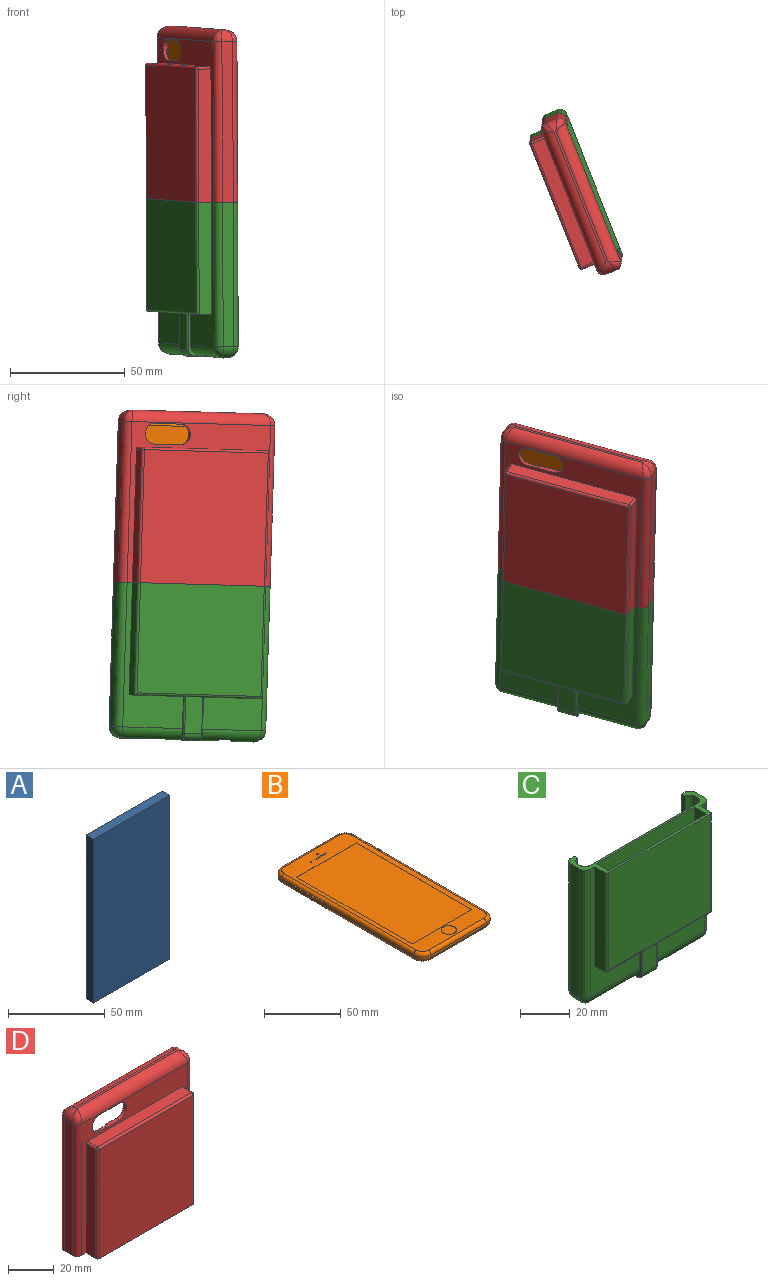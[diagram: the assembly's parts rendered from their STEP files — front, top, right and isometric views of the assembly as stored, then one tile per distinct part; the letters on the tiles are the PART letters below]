
ASSEMBLY  parts=4 mates=4
PART A: 11 faces, bbox 55.5x5.5x103.5 mm
  f0: plane 55.5x5.5mm, normal (0,0,-1), area 279mm2, adj f2,f3,f4,f5,f6,f7,f8,f9
  f1: plane 55.5x5.5mm, normal (0,0,1), area 305.2mm2, adj f2,f3,f4,f5
  f2: plane 103.5x5.5mm, normal (-1,0,0), area 569.2mm2, adj f0,f1,f4,f5
  f3: plane 103.5x5.5mm, normal (1,0,0), area 569.2mm2, adj f0,f1,f4,f5
  f4: plane 103.5x55.5mm, normal (0,-1,0), area 5744.2mm2, adj f0,f1,f2,f3
  f5: plane 103.5x55.5mm, normal (0,1,0), area 5744.2mm2, adj f0,f1,f2,f3
  f6: plane 7.5x7.5mm, normal (0,1,0), area 56.2mm2, adj f0,f7,f9,f10
  f7: plane 7.5x3.5mm, normal (1,0,0), area 26.2mm2, adj f0,f6,f8,f10
  f8: plane 7.5x7.5mm, normal (0,-1,0), area 56.2mm2, adj f0,f7,f9,f10
  f9: plane 7.5x3.5mm, normal (-1,0,0), area 26.2mm2, adj f0,f6,f8,f10
  f10: plane 7.5x3.5mm, normal (0,0,-1), area 26.2mm2, adj f6,f7,f8,f9
PART B: 83 faces, bbox 69x139.3x7 mm
  f0: plane 12.52x2.01mm, normal (-1,0,0), area 24.1mm2, adj f6,f41,f53,f75,f76,f77
  f1: plane 2.92x2.01mm, normal (-1,0,0), area 4.3mm2, adj f41,f53,f64,f65,f66,f79,f80,f81
  f2: plane 97.29x2mm, normal (1,0,0), area 194.1mm2, adj f21,f34,f35,f36,f42,f54
  f3: plane 12.29x2mm, normal (1,0,0), area 24.1mm2, adj f4,f30,f31,f32,f49,f61
  f4: cylinder r=8mm len=8mm, axis (0,0,-1), area 25.1mm2, adj f3,f5,f47,f59
  f5: plane 51x2mm, normal (0,1,0), area 102mm2, adj f4,f6,f45,f57
  f6: cylinder r=8mm len=8mm, axis (0,0,-1), area 25.1mm2, adj f0,f5,f43,f55
  f7: plane 79.91x2mm, normal (-1,0,0), area 159.1mm2, adj f8,f41,f53,f68,f69,f70
  f8: cylinder r=8mm len=8mm, axis (0,0,-1), area 25.1mm2, adj f7,f9,f39,f51
  f9: plane 51x2mm, normal (0,-1,0), area 102mm2, adj f8,f21,f38,f50
  f10: plane 1x0.05mm, normal (1,0,0), area 0.1mm2, adj f11,f16,f22,f26
  f11: plane 10x0.05mm, normal (0,-1,0), area 0.5mm2, adj f10,f12,f22,f26
  f12: plane 1x0.05mm, normal (-1,0,0), area 0.1mm2, adj f11,f16,f22,f26
  f13: plane 55x0.05mm, normal (0,1,0), area 2.8mm2, adj f14,f20,f22,f24
  f14: plane 106.54x0.05mm, normal (1,0,0), area 5.3mm2, adj f13,f15,f22,f24
  f15: plane 55x0.05mm, normal (0,-1,0), area 2.8mm2, adj f14,f20,f22,f24
  f16: plane 10x0.05mm, normal (0,1,0), area 0.5mm2, adj f10,f12,f22,f26
  f17: cylinder r=5mm len=10mm, axis (0,0,-1), area 1.6mm2, adj f22,f25
  f18: cylinder r=0.5mm len=1mm, axis (0,0,-1), area 0.2mm2, adj f22,f27
  f19: cylinder r=0.5mm len=1mm, axis (0,0,-1), area 0.2mm2, adj f22,f28
  f20: plane 106.5x0.05mm, normal (-1,0,0), area 5.3mm2, adj f13,f15,f22,f24
  f21: cylinder r=8mm len=8mm, axis (0,0,-1), area 25.1mm2, adj f2,f9,f40,f52
  f22: plane 133x62.03mm, normal (0,0,1), area 2271.7mm2, adj f10,f11,f12,f13,f14,f15,f16,f17
  f23: plane 133x62.02mm, normal (0,0,-1), area 8220.2mm2, adj f50,f51,f52,f53,f54,f55,f56,f57
  f24: plane 106.54x55mm, normal (0,0,1), area 5858.6mm2, adj f13,f14,f15,f20
  f25: plane 10x10mm, normal (0,0,1), area 78.5mm2, adj f17
  f26: plane 10x1mm, normal (0,0,1), area 10mm2, adj f10,f11,f12,f16
  f27: plane 1x1mm, normal (0,0,1), area 0.8mm2, adj f18
  f28: plane 1x1mm, normal (0,0,1), area 0.8mm2, adj f19
  f29: plane 11x1mm, normal (0,0,-1), area 11mm2, adj f30,f36,f37,f58
  f30: cylinder r=1mm len=1mm, axis (-1,0,0), area 1.6mm2, adj f3,f29,f31,f37,f60
  f31: plane 1x0.7mm, normal (0,1,0), area 0.7mm2, adj f3,f30,f32,f37
  f32: cylinder r=1mm len=1mm, axis (-1,0,0), area 1.6mm2, adj f3,f31,f33,f37,f48
  f33: plane 11x1mm, normal (0,0,1), area 11mm2, adj f32,f34,f37,f46
  f34: cylinder r=1mm len=1mm, axis (-1,0,0), area 1.6mm2, adj f2,f33,f35,f37,f44
  f35: plane 1x0.7mm, normal (0,-1,0), area 0.7mm2, adj f2,f34,f36,f37
  f36: cylinder r=1mm len=1mm, axis (-1,0,0), area 1.6mm2, adj f2,f29,f35,f37,f56
  f37: plane 13x2.7mm, normal (1,0,0), area 34.2mm2, adj f29,f30,f31,f32,f33,f34,f35,f36
  f38: cylinder r=2.5mm len=51mm, axis (-1,0,0), area 200.3mm2, adj f9,f22,f39,f40
  f39: torus R=5.5mm, axis (0,0,1), area 43.7mm2, adj f8,f22,f38,f41
  f40: torus R=5.5mm, axis (0,0,1), area 43.7mm2, adj f21,f22,f38,f42
  f41: cylinder r=2.5mm len=122mm, axis (0,1,0), area 479.1mm2, adj f0,f1,f7,f22,f39,f43,f62,f73
  f42: cylinder r=2.5mm len=97.2mm, axis (0,-1,0), area 381.7mm2, adj f2,f22,f40,f44
  f43: torus R=5.5mm, axis (0,0,1), area 43.7mm2, adj f6,f22,f41,f45
  f44: bspline ~2.55x2.54mm, area 2.9mm2, adj f22,f34,f42,f46
  f45: cylinder r=2.5mm len=51mm, axis (1,0,0), area 200.3mm2, adj f5,f22,f43,f47
  f46: cylinder r=2.5mm len=11mm, axis (0,1,0), area 38.8mm2, adj f22,f33,f44,f48
  f47: torus R=5.5mm, axis (0,0,1), area 43.7mm2, adj f4,f22,f45,f49
  f48: bspline ~2.57x2.57mm, area 2.9mm2, adj f22,f32,f46,f49
  f49: cylinder r=2.5mm len=12.2mm, axis (0,-1,0), area 47.9mm2, adj f3,f22,f47,f48
  f50: cylinder r=2.5mm len=51mm, axis (1,0,0), area 200.3mm2, adj f9,f23,f51,f52
  f51: torus R=5.5mm, axis (0,0,1), area 43.7mm2, adj f8,f23,f50,f53
  f52: torus R=5.5mm, axis (0,0,1), area 43.7mm2, adj f21,f23,f50,f54
  f53: cylinder r=2.5mm len=122mm, axis (0,-1,0), area 477.5mm2, adj f0,f1,f7,f23,f51,f55,f72,f77
  f54: cylinder r=2.5mm len=97.29mm, axis (0,1,0), area 382mm2, adj f2,f23,f52,f56
  f55: torus R=5.5mm, axis (0,0,1), area 43.7mm2, adj f6,f23,f53,f57
  f56: bspline ~2.67x2.66mm, area 2.7mm2, adj f23,f36,f54,f58
  f57: cylinder r=2.5mm len=51mm, axis (-1,0,0), area 200.3mm2, adj f5,f23,f55,f59
  f58: cylinder r=2.5mm len=11mm, axis (0,1,0), area 39.9mm2, adj f23,f29,f56,f60
  f59: torus R=5.5mm, axis (0,0,1), area 43.7mm2, adj f4,f23,f57,f61
  f60: bspline ~2.57x2.56mm, area 2.7mm2, adj f23,f30,f58,f61
  f61: cylinder r=2.5mm len=12.29mm, axis (0,1,0), area 48.2mm2, adj f3,f23,f59,f60
  f62: plane 14.23x0.5mm, normal (1,0,0), area 6.9mm2, adj f41,f63,f64,f70
  f63: plane 12.49x1mm, normal (0,0,1), area 12.5mm2, adj f62,f64,f70,f71
  f64: cylinder r=1mm len=1mm, axis (1,0,0), area 1.6mm2, adj f1,f62,f63,f65,f71
  f65: plane 1x0.7mm, normal (0,1,0), area 0.7mm2, adj f1,f64,f66,f71
  f66: cylinder r=1mm len=1mm, axis (1,0,0), area 1.6mm2, adj f1,f65,f67,f71,f72
  f67: plane 12.49x1mm, normal (0,0,-1), area 12.5mm2, adj f66,f68,f71,f72
  f68: cylinder r=1mm len=1mm, axis (1,0,0), area 1.6mm2, adj f7,f67,f69,f71,f72
  f69: plane 1x0.7mm, normal (0,-1,0), area 0.7mm2, adj f7,f68,f70,f71
  f70: cylinder r=1mm len=1mm, axis (1,0,0), area 1.6mm2, adj f7,f62,f63,f69,f71
  f71: plane 14.49x2.7mm, normal (-1,0,0), area 38.3mm2, adj f63,f64,f65,f66,f67,f68,f69,f70
  f72: plane 13.69x0.2mm, normal (1,0,0), area 2.7mm2, adj f53,f66,f67,f68
  f73: plane 13.81x0.57mm, normal (1,0,0), area 7.6mm2, adj f41,f74,f75,f81
  f74: plane 12x1mm, normal (0,0,1), area 12mm2, adj f73,f75,f81,f82
  f75: cylinder r=1mm len=1mm, axis (1,0,0), area 1.6mm2, adj f0,f73,f74,f76,f82
  f76: plane 1x0.7mm, normal (0,1,0), area 0.7mm2, adj f0,f75,f77,f82
  f77: cylinder r=1mm len=1mm, axis (1,0,0), area 1.6mm2, adj f0,f53,f76,f78,f82
  f78: plane 12.01x1.01mm, normal (0,0,-1), area 12mm2, adj f53,f77,f79,f82
  f79: cylinder r=1mm len=1mm, axis (1,0,0), area 1.6mm2, adj f1,f53,f78,f80,f82
  f80: plane 1x0.7mm, normal (0,-1,0), area 0.7mm2, adj f1,f79,f81,f82
  f81: cylinder r=1mm len=1mm, axis (1,0,0), area 1.6mm2, adj f1,f73,f74,f80,f82
  f82: plane 14x2.7mm, normal (-1,0,0), area 36.9mm2, adj f74,f75,f76,f77,f78,f79,f80,f81
PART C: 93 faces, bbox 71x18x68.2 mm
  f0: cylinder r=5mm len=28.5mm, axis (1,0,0), area 188.9mm2, adj f5,f7,f28,f33,f52,f53,f54,f83
  f1: plane 63x28mm, normal (0,-1,0), area 514.5mm2, adj f2,f4,f10,f25,f66,f84
  f2: plane 60x6mm, normal (0,0,-1), area 346.6mm2, adj f1,f5,f65,f66,f82,f83,f84,f85
  f3: plane 56x7mm, normal (0,0,1), area 382.5mm2, adj f64,f67,f68,f69,f70,f71,f72,f73
  f4: plane 71x18mm, normal (0,0,1), area 217.6mm2, adj f1,f5,f11,f12,f13,f14,f15,f16
  f5: plane 63x28mm, normal (0,-1,0), area 514.5mm2, adj f0,f2,f4,f24,f65,f83
  f6: plane 67x7mm, normal (0,0,1), area 383.7mm2, adj f14,f15,f16,f17,f18,f19,f20,f35
  f7: plane 23x4.5mm, normal (0,0,-1), area 51mm2, adj f0,f9,f10,f46,f52,f86,f87,f91
  f8: plane 9x1mm, normal (0,0,-1), area 9mm2, adj f9,f10,f29,f48
  f9: cylinder r=5mm len=65mm, axis (-1,0,0), area 452.3mm2, adj f7,f8,f13,f21,f28,f30,f32,f36
  f10: cylinder r=5mm len=28.5mm, axis (1,0,0), area 193.8mm2, adj f1,f7,f8,f31,f46,f48,f49,f84
  f11: plane 63x2mm, normal (-1,0,0), area 126mm2, adj f4,f13,f14,f36
  f12: plane 63x2mm, normal (1,0,0), area 126mm2, adj f4,f20,f21,f36
  f13: plane 63x2mm, normal (0,1,0), area 126mm2, adj f4,f9,f11,f27
  f14: cylinder r=3mm len=65mm, axis (0,0,1), area 306.3mm2, adj f4,f6,f11,f15,f35
  f15: plane 65x1mm, normal (-1,0,0), area 65mm2, adj f4,f6,f14,f16
  f16: cylinder r=3mm len=65mm, axis (0,0,1), area 306.3mm2, adj f4,f6,f15,f17
  f17: plane 65x61mm, normal (0,1,0), area 3965mm2, adj f4,f6,f16,f18
  f18: cylinder r=3mm len=65mm, axis (0,0,1), area 306.3mm2, adj f4,f6,f17,f19
  f19: plane 65x1mm, normal (1,0,0), area 65mm2, adj f4,f6,f18,f20
  f20: cylinder r=3mm len=65mm, axis (0,0,1), area 306.3mm2, adj f4,f6,f12,f19,f35
  f21: plane 63x2mm, normal (0,1,0), area 126mm2, adj f4,f9,f12,f22
  f22: cylinder r=3mm len=63mm, axis (0,0,1), area 296.9mm2, adj f4,f21,f23,f32
  f23: plane 63x5mm, normal (-1,0,0), area 315mm2, adj f4,f22,f24,f34
  f24: cylinder r=3mm len=63mm, axis (0,0,1), area 296.9mm2, adj f4,f5,f23,f33
  f25: cylinder r=3mm len=63mm, axis (0,0,1), area 296.9mm2, adj f1,f4,f26,f31
  f26: plane 63x5mm, normal (1,0,0), area 315mm2, adj f4,f25,f27,f29
  f27: cylinder r=3mm len=63mm, axis (0,0,1), area 296.9mm2, adj f4,f13,f26,f30
  f28: plane 4x1mm, normal (0,0,-1), area 4mm2, adj f0,f9,f34,f54
  f29: cylinder r=5mm len=5mm, axis (0,1,0), area 27.9mm2, adj f8,f26,f30,f31
  f30: bspline ~6.03x5mm, area 24.5mm2, adj f9,f27,f29
  f31: bspline ~6.03x5mm, area 24.5mm2, adj f10,f25,f29
  f32: bspline ~6.03x5mm, area 24.5mm2, adj f9,f22,f34
  f33: bspline ~6.03x5mm, area 24.5mm2, adj f0,f24,f34
  f34: cylinder r=5mm len=5mm, axis (0,-1,0), area 27.9mm2, adj f23,f28,f32,f33
  f35: plane 61x2mm, normal (0,-1,0), area 122mm2, adj f6,f14,f20,f36
  f36: plane 61x2mm, normal (0,0,1), area 122mm2, adj f9,f11,f12,f35
  f37: plane 6x5.5mm, normal (0,1,0), area 33mm2, adj f6,f38,f44,f45
  f38: cylinder r=0.5mm len=6mm, axis (0,0,-1), area 4.7mm2, adj f6,f37,f39,f45
  f39: plane 6x0.5mm, normal (-1,0,0), area 3mm2, adj f6,f38,f40,f45
  f40: cylinder r=0.5mm len=6mm, axis (0,0,-1), area 4.7mm2, adj f6,f39,f41,f45
  f41: plane 6x5.5mm, normal (0,-1,0), area 33mm2, adj f6,f40,f42,f45
  f42: cylinder r=0.5mm len=6mm, axis (0,0,-1), area 4.7mm2, adj f6,f41,f43,f45
  f43: plane 6x0.5mm, normal (1,0,0), area 3mm2, adj f6,f42,f44,f45
  f44: cylinder r=0.5mm len=6mm, axis (0,0,-1), area 4.7mm2, adj f6,f37,f43,f45
  f45: plane 6.5x1.5mm, normal (0,0,1), area 9.5mm2, adj f37,f38,f39,f40,f41,f42,f43,f44
  f46: plane 6x1mm, normal (1,0,0), area 4.9mm2, adj f7,f9,f10,f47,f49,f50
  f47: plane 8x0.33mm, normal (0,-1,0), area 2.6mm2, adj f9,f46,f48,f50
  f48: plane 6x1mm, normal (-1,0,0), area 4.9mm2, adj f8,f9,f10,f47,f49,f50
  f49: plane 8x0.33mm, normal (0,1,0), area 2.6mm2, adj f10,f46,f48,f50
  f50: plane 8x6mm, normal (0,0,-1), area 18.7mm2, adj f46,f47,f48,f49,f60,f61,f62,f63
  f51: plane 17x0.77mm, normal (0,-1,0), area 13.1mm2, adj f9,f52,f54,f55
  f52: plane 4x1mm, normal (-1,0,0), area 3.8mm2, adj f0,f7,f9,f51,f53,f55
  f53: plane 17x0.77mm, normal (0,1,0), area 13.1mm2, adj f0,f52,f54,f55
  f54: plane 4x1mm, normal (1,0,0), area 3.8mm2, adj f0,f9,f28,f51,f53,f55
  f55: plane 17x4mm, normal (0,0,-1), area 29.3mm2, adj f51,f52,f53,f54,f56,f57,f58,f59
  f56: plane 15.5x2mm, normal (0,-1,0), area 31mm2, adj f6,f55,f58,f59
  f57: plane 15.5x2mm, normal (0,1,0), area 31mm2, adj f6,f55,f58,f59
  f58: plane 2.5x2mm, normal (-1,0,0), area 5mm2, adj f6,f55,f56,f57
  f59: plane 2.5x2mm, normal (1,0,0), area 5mm2, adj f6,f55,f56,f57
  f60: plane 6.5x2mm, normal (0,1,0), area 13mm2, adj f6,f50,f62,f63
  f61: plane 6.5x2mm, normal (0,-1,0), area 13mm2, adj f6,f50,f62,f63
  f62: plane 4.5x2mm, normal (1,0,0), area 9mm2, adj f6,f50,f60,f61
  f63: plane 4.5x2mm, normal (-1,0,0), area 9mm2, adj f6,f50,f60,f61
  f64: plane 47x7mm, normal (1,0,0), area 329mm2, adj f3,f4,f68,f79
  f65: plane 49x6mm, normal (-1,0,0), area 294mm2, adj f2,f4,f5,f80
  f66: plane 49x6mm, normal (1,0,0), area 294mm2, adj f1,f2,f4,f81
  f67: plane 47x7mm, normal (-1,0,0), area 329mm2, adj f3,f4,f68,f79
  f68: plane 56x47mm, normal (0,-1,0), area 2632mm2, adj f3,f4,f64,f67
  f69: plane 6x5.5mm, normal (0,1,0), area 33mm2, adj f3,f70,f76,f77
  f70: cylinder r=0.5mm len=6mm, axis (0,0,-1), area 4.7mm2, adj f3,f69,f71,f77
  f71: plane 6x0.5mm, normal (-1,0,0), area 3mm2, adj f3,f70,f72,f77
  f72: cylinder r=0.5mm len=6mm, axis (0,0,-1), area 4.7mm2, adj f3,f71,f73,f77
  f73: plane 6x5.5mm, normal (0,-1,0), area 33mm2, adj f3,f72,f74,f77
  f74: cylinder r=0.5mm len=6mm, axis (0,0,-1), area 4.7mm2, adj f3,f73,f75,f77
  f75: plane 6x0.5mm, normal (1,0,0), area 3mm2, adj f3,f74,f76,f77
  f76: cylinder r=0.5mm len=6mm, axis (0,0,-1), area 4.7mm2, adj f3,f69,f75,f77
  f77: plane 6.5x1.5mm, normal (0,0,1), area 9.5mm2, adj f69,f70,f71,f72,f73,f74,f75,f76
  f78: plane 58x48mm, normal (0,-1,0), area 2784mm2, adj f4,f80,f81,f82
  f79: plane 56x47mm, normal (0,1,0), area 2632mm2, adj f3,f4,f64,f67
  f80: cylinder r=1mm len=49mm, axis (0,0,1), area 76.4mm2, adj f4,f65,f78,f82
  f81: cylinder r=1mm len=49mm, axis (0,0,-1), area 76.4mm2, adj f4,f66,f78,f82
  f82: cylinder r=1mm len=60mm, axis (-1,0,0), area 93.1mm2, adj f2,f78,f80,f81
  f83: plane 18.5x3.82mm, normal (-1,0,0), area 20.8mm2, adj f0,f2,f5,f87,f88,f89
  f84: plane 18.5x3.82mm, normal (1,0,0), area 20.8mm2, adj f1,f2,f10,f90,f91,f92
  f85: plane 16x8mm, normal (0,-1,0), area 128mm2, adj f2,f86,f88,f90
  f86: cylinder r=3mm len=8mm, axis (1,0,0), area 37.7mm2, adj f7,f85,f89,f92
  f87: cylinder r=0.5mm len=3.5mm, axis (0,-1,0), area 1.9mm2, adj f0,f7,f83,f89
  f88: cylinder r=0.5mm len=16mm, axis (0,0,1), area 12.6mm2, adj f2,f83,f85,f89
  f89: torus R=2.5mm, axis (1,0,0), area 3.5mm2, adj f83,f86,f87,f88
  f90: cylinder r=0.5mm len=16mm, axis (0,0,-1), area 12.6mm2, adj f2,f84,f85,f92
  f91: cylinder r=0.5mm len=3.5mm, axis (0,1,0), area 1.9mm2, adj f7,f10,f84,f92
  f92: torus R=2.5mm, axis (1,0,0), area 3.5mm2, adj f84,f86,f90,f91
PART D: 54 faces, bbox 71x18x75 mm
  f0: plane 73x61mm, normal (0,1,0), area 3671.2mm2, adj f1,f2,f9,f10,f20,f48,f49,f50
  f1: plane 12.1x2mm, normal (0,0,1), area 21.4mm2, adj f0,f5,f48,f50,f52,f53
  f2: plane 67x7mm, normal (0,0,-1), area 461.3mm2, adj f0,f7,f8,f9,f10,f11,f12,f40
  f3: plane 70.5x2mm, normal (1,0,0), area 141mm2, adj f4,f12,f20,f38,f39
  f4: plane 70x2mm, normal (0,1,0), area 140mm2, adj f3,f14,f20,f38
  f5: plane 70x65mm, normal (0,-1,0), area 837.9mm2, adj f1,f16,f17,f20,f25,f26,f27,f31
  f6: plane 70.5x2mm, normal (-1,0,0), area 141mm2, adj f7,f13,f20,f38,f39
  f7: cylinder r=3mm len=73mm, axis (0,0,-1), area 344mm2, adj f2,f6,f8,f20,f40
  f8: plane 73x1mm, normal (-1,0,0), area 73mm2, adj f2,f7,f9,f20
  f9: cylinder r=3mm len=73mm, axis (0,0,-1), area 344mm2, adj f0,f2,f8,f20
  f10: cylinder r=3mm len=73mm, axis (0,0,-1), area 344mm2, adj f0,f2,f11,f20
  f11: plane 73x1mm, normal (1,0,0), area 73mm2, adj f2,f10,f12,f20
  f12: cylinder r=3mm len=73mm, axis (0,0,-1), area 344mm2, adj f2,f3,f11,f20,f40
  f13: plane 70x2mm, normal (0,1,0), area 140mm2, adj f6,f19,f20,f38
  f14: cylinder r=3mm len=70mm, axis (0,0,-1), area 329.9mm2, adj f4,f15,f20,f37
  f15: plane 70x5mm, normal (-1,0,0), area 350mm2, adj f14,f16,f20,f35
  f16: cylinder r=3mm len=70mm, axis (0,0,-1), area 329.9mm2, adj f5,f15,f20,f33
  f17: cylinder r=3mm len=70mm, axis (0,0,-1), area 329.9mm2, adj f5,f18,f20,f32
  f18: plane 70x5mm, normal (1,0,0), area 350mm2, adj f17,f19,f20,f34
  f19: cylinder r=3mm len=70mm, axis (0,0,-1), area 329.9mm2, adj f13,f18,f20,f36
  f20: plane 71x18mm, normal (0,0,-1), area 212.6mm2, adj f0,f3,f4,f5,f6,f7,f8,f9
  f21: plane 61x1mm, normal (0,0,1), area 61mm2, adj f31,f34,f35,f38
  f22: plane 57x7mm, normal (1,0,0), area 399mm2, adj f20,f23,f28,f29
  f23: plane 56x7mm, normal (0,0,-1), area 392mm2, adj f22,f24,f28,f29
  f24: plane 57x7mm, normal (-1,0,0), area 399mm2, adj f20,f23,f28,f29
  f25: plane 58x6mm, normal (1,0,0), area 348mm2, adj f5,f20,f45,f47
  f26: plane 58x6mm, normal (0,0,1), area 348mm2, adj f5,f42,f44,f45
  f27: plane 58x6mm, normal (-1,0,0), area 348mm2, adj f5,f20,f41,f42
  f28: plane 57x56mm, normal (0,-1,0), area 3192mm2, adj f20,f22,f23,f24
  f29: plane 57x56mm, normal (0,1,0), area 3192mm2, adj f20,f22,f23,f24
  f30: plane 58x58mm, normal (0,-1,0), area 3364mm2, adj f20,f41,f44,f47
  f31: cylinder r=5mm len=65mm, axis (-1,0,0), area 499.1mm2, adj f5,f21,f32,f33
  f32: bspline ~6.03x5mm, area 24.5mm2, adj f17,f31,f34
  f33: bspline ~6.03x5mm, area 24.5mm2, adj f16,f31,f35
  f34: cylinder r=5mm len=5mm, axis (0,-1,0), area 27.9mm2, adj f18,f21,f32,f36
  f35: cylinder r=5mm len=5mm, axis (0,1,0), area 27.9mm2, adj f15,f21,f33,f37
  f36: bspline ~5.26x5mm, area 24.5mm2, adj f19,f34,f38
  f37: bspline ~6.03x5mm, area 24.5mm2, adj f14,f35,f38
  f38: cylinder r=5mm len=65mm, axis (-1,0,0), area 468.5mm2, adj f3,f4,f6,f13,f21,f36,f37,f39
  f39: plane 61x1.98mm, normal (0,0,-1), area 120.5mm2, adj f3,f6,f38,f40
  f40: plane 61x2.5mm, normal (0,-1,0), area 152.5mm2, adj f2,f7,f12,f39
  f41: cylinder r=1mm len=58mm, axis (0,0,1), area 91.1mm2, adj f20,f27,f30,f43
  f42: cylinder r=1mm len=6mm, axis (0,1,0), area 9.4mm2, adj f5,f26,f27,f43
  f43: sphere r=1mm, area 1.6mm2, adj f41,f42,f44
  f44: cylinder r=1mm len=58mm, axis (1,0,0), area 91.1mm2, adj f26,f30,f43,f46
  f45: cylinder r=1mm len=6mm, axis (0,-1,0), area 9.4mm2, adj f5,f25,f26,f46
  f46: sphere r=1mm, area 1.6mm2, adj f44,f45,f47
  f47: cylinder r=1mm len=58mm, axis (0,0,-1), area 91.1mm2, adj f20,f25,f30,f46
  f48: cylinder r=4.5mm len=9mm, axis (0,-1,0), area 28.3mm2, adj f0,f1,f5,f49
  f49: plane 12.1x2mm, normal (0,0,-1), area 24.2mm2, adj f0,f5,f48,f50
  f50: cylinder r=4.5mm len=9mm, axis (0,-1,0), area 24.7mm2, adj f0,f1,f5,f49,f51,f53
  f51: plane 65x0.5mm, normal (1,0,0), area 32.5mm2, adj f0,f20,f50,f53
  f52: plane 60.5x0.5mm, normal (-1,0,0), area 30.2mm2, adj f0,f1,f20,f53
  f53: plane 65x10mm, normal (0,1,0), area 609.3mm2, adj f1,f20,f50,f51,f52
PLACE A rot(axis=(0.02,0.01,-1),68.3deg) t=(-250.55,-47.99,58.2)mm
PLACE B rot(axis=(0.44,0.63,0.65),133.8deg) t=(-248.96,-46.54,41.19)mm
PLACE C rot(axis=(0.02,0.01,-1),68.3deg) t=(-245.65,-45.89,53.03)mm fixed
PLACE D rot(axis=(0.02,0.01,-1),68.3deg) t=(-245.53,-45.85,53.03)mm
MATE slider D.f20 <-> C.f4  axis (0,-0.03,1) through (-231.12,-72.93,52.27)mm
MATE slider A.f1 <-> D.f23  axis (0,-0.03,1) through (-253.32,-50.57,109.88)mm
MATE planar B.f23 <-> D.f0  axis (-0.93,-0.37,-0.02) through (-249.02,-46.96,55.04)mm
MATE slider A.f0 <-> C.f3  axis (0,0.03,-1) through (-252.88,-47.44,6.43)mm
